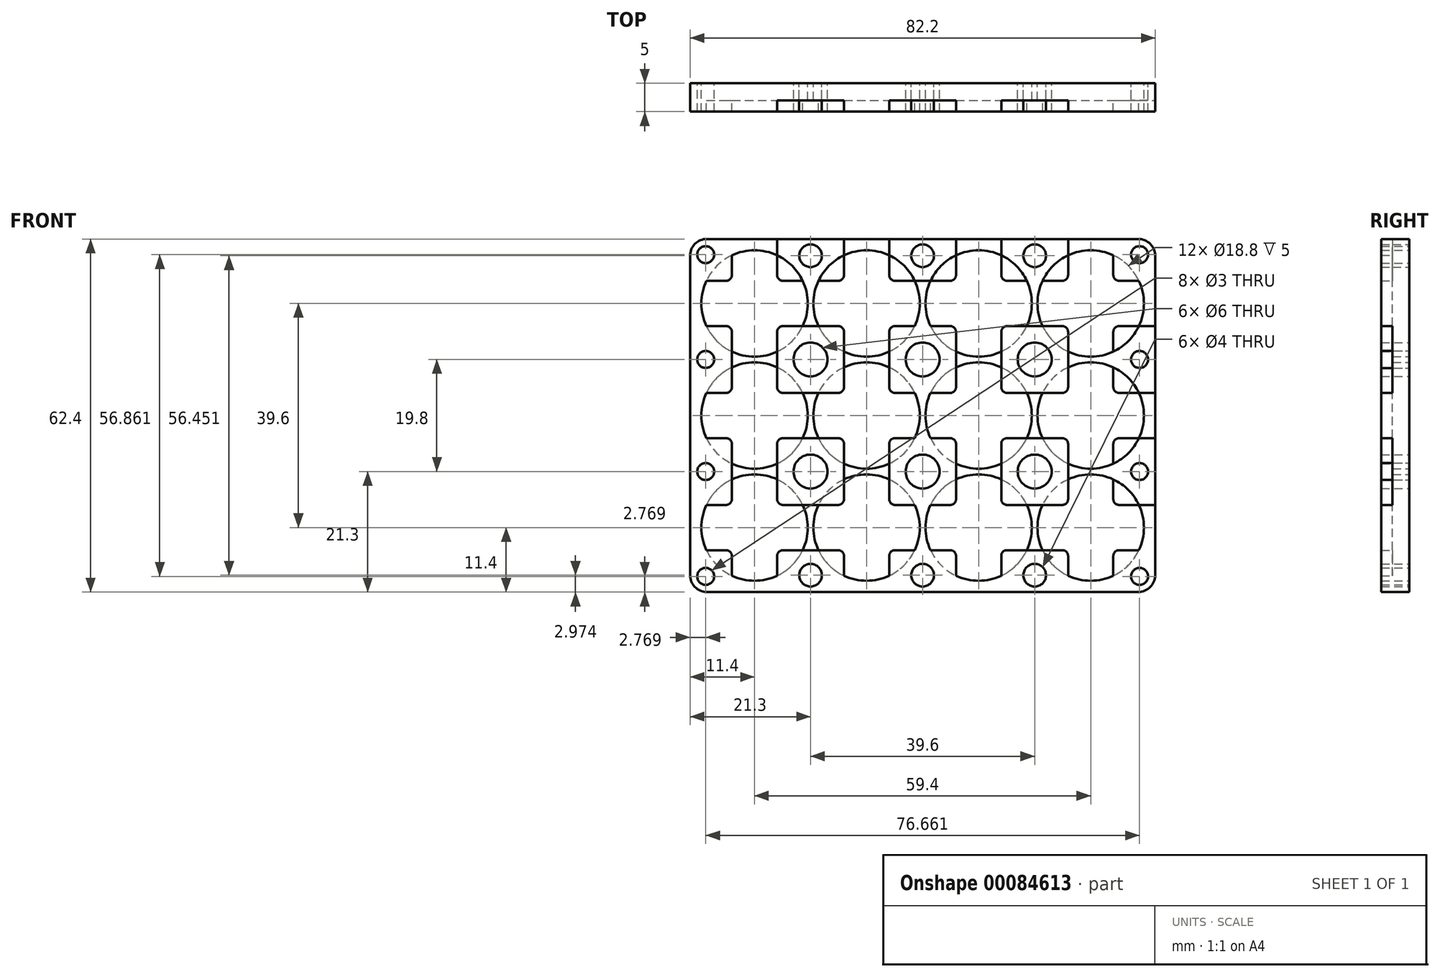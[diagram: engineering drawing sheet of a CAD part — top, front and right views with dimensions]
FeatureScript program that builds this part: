
annotation { "Feature Type Name" : "Feature", "Feature Type Description" : "" }
export const myFeature = defineFeature(function(context is Context, id is Id, definition is map)
    precondition{}
    {
        {
            var Q0;
            Q0=qCreatedBy(makeId("Front.planeOp"),FACE);
            var sketch = newSketch(context, id + "F0", { "sketchPlane" : qUnion([Q0]) });
            skCircle(sketch, "E0", {"center": v(0, 0) * mm, "radius": 9.4 * mm});
            skCircle(sketch, "E1.0.1.0", {"center": v(0, 19.8) * mm, "radius": 9.4 * mm});
            skCircle(sketch, "E1.0.2.0", {"center": v(0, 39.6) * mm, "radius": 9.4 * mm});
            skCircle(sketch, "E1.1.0.0", {"center": v(19.8, 0) * mm, "radius": 9.4 * mm});
            skCircle(sketch, "E1.1.1.0", {"center": v(19.8, 19.8) * mm, "radius": 9.4 * mm});
            skCircle(sketch, "E1.1.2.0", {"center": v(19.8, 39.6) * mm, "radius": 9.4 * mm});
            skCircle(sketch, "E1.2.0.0", {"center": v(39.6, 0) * mm, "radius": 9.4 * mm});
            skCircle(sketch, "E1.2.1.0", {"center": v(39.6, 19.8) * mm, "radius": 9.4 * mm});
            skCircle(sketch, "E1.2.2.0", {"center": v(39.6, 39.6) * mm, "radius": 9.4 * mm});
            skCircle(sketch, "E1.3.0.0", {"center": v(59.4, 0) * mm, "radius": 9.4 * mm});
            skCircle(sketch, "E1.3.1.0", {"center": v(59.4, 19.8) * mm, "radius": 9.4 * mm});
            skCircle(sketch, "E1.3.2.0", {"center": v(59.4, 39.6) * mm, "radius": 9.4 * mm});
            skLineSegment(sketch, "E1.direction1", {"start": v(0, 0) * mm, "end": v(19.8, 0) * mm, "construction": true});
            skLineSegment(sketch, "E1.direction2", {"start": v(0, 0) * mm, "end": v(0, 19.8) * mm, "construction": true});
            skLineSegment(sketch, "E2", {"start": v(-9.4, 19.8) * mm, "end": v(68.8, 19.8) * mm, "construction": true});
            skLineSegment(sketch, "E3", {"start": v(29.7, 19.8) * mm, "end": v(29.7, -16.3) * mm, "construction": true});
            skLineSegment(sketch, "E4.bottom", {"start": v(70.8, -11.4) * mm, "end": v(-11.4, -11.4) * mm});
            skLineSegment(sketch, "E4.top", {"start": v(70.8, 51) * mm, "end": v(-11.4, 51) * mm});
            skLineSegment(sketch, "E4.left", {"start": v(70.8, -11.4) * mm, "end": v(70.8, 51) * mm});
            skLineSegment(sketch, "E4.right", {"start": v(-11.4, -11.4) * mm, "end": v(-11.4, 51) * mm});
            skPoint(sketch, "E4.middle", {"position": v(29.7, 19.8) * mm});
            skLineSegment(sketch, "E5", {"start": v(19.8, 19.8) * mm, "end": v(0, 0) * mm, "construction": true});
            skLineSegment(sketch, "E6", {"start": v(19.8, 0) * mm, "end": v(0, 19.8) * mm, "construction": true});
            skCircle(sketch, "E7", {"center": v(9.9, 9.9) * mm, "radius": 3 * mm});
            skCircle(sketch, "E8.0.1.0", {"center": v(9.9, 29.7) * mm, "radius": 3 * mm});
            skCircle(sketch, "E8.1.0.0", {"center": v(29.7, 9.9) * mm, "radius": 3 * mm});
            skCircle(sketch, "E8.1.1.0", {"center": v(29.7, 29.7) * mm, "radius": 3 * mm});
            skCircle(sketch, "E8.2.0.0", {"center": v(49.5, 9.9) * mm, "radius": 3 * mm});
            skCircle(sketch, "E8.2.1.0", {"center": v(49.5, 29.7) * mm, "radius": 3 * mm});
            skLineSegment(sketch, "E8.direction1", {"start": v(9.9, 9.9) * mm, "end": v(29.7, 9.9) * mm, "construction": true});
            skLineSegment(sketch, "E8.direction2", {"start": v(9.9, 9.9) * mm, "end": v(9.9, 29.7) * mm, "construction": true});
            skLineSegment(sketch, "E9", {"start": v(9.9, 0) * mm, "end": v(9.9, -11.4) * mm, "construction": true});
            skCircle(sketch, "E10", {"center": v(9.9, -8.43) * mm, "radius": 2 * mm});
            skCircle(sketch, "E11.1.0.0", {"center": v(29.7, -8.43) * mm, "radius": 2 * mm});
            skCircle(sketch, "E11.2.0.0", {"center": v(49.5, -8.43) * mm, "radius": 2 * mm});
            skLineSegment(sketch, "E11.direction1", {"start": v(9.9, -8.43) * mm, "end": v(29.7, -8.43) * mm, "construction": true});
            skCircle(sketch, "E12.MirrorC", {"center": v(9.9, 48.03) * mm, "radius": 2 * mm});
            skCircle(sketch, "E13.MirrorC", {"center": v(29.7, 48.03) * mm, "radius": 2 * mm});
            skCircle(sketch, "E14.MirrorC", {"center": v(49.5, 48.03) * mm, "radius": 2 * mm});
            skLineSegment(sketch, "E15", {"start": v(0, 0) * mm, "end": v(-11.4, -11.4) * mm, "construction": true});
            skCircle(sketch, "E16", {"center": v(-8.63, -8.63) * mm, "radius": 1.5 * mm});
            skCircle(sketch, "E17", {"center": v(-8.63, 9.9) * mm, "radius": 1.5 * mm});
            skCircle(sketch, "E18", {"center": v(-8.63, 29.7) * mm, "radius": 1.5 * mm});
            skCircle(sketch, "E19.MirrorC", {"center": v(-8.63, 48.23) * mm, "radius": 1.5 * mm});
            skCircle(sketch, "E20.MirrorC", {"center": v(68.03, -8.63) * mm, "radius": 1.5 * mm});
            skCircle(sketch, "E21.MirrorC", {"center": v(68.03, 9.9) * mm, "radius": 1.5 * mm});
            skCircle(sketch, "E22.MirrorC", {"center": v(68.03, 29.7) * mm, "radius": 1.5 * mm});
            skCircle(sketch, "E23.MirrorC", {"center": v(68.03, 48.23) * mm, "radius": 1.5 * mm});
            skSolve(sketch);
        }
        {
            var Q0;
            Q0=qSketchRegion(id+"F0",true);
            extrude(context, id + "F1", {"entities" : qUnion([Q0]), "depth" : 3 * mm});
        }
        {
            var Q0;
            Q0=makeQuery(id+"F1.opExtrude","SWEPT_EDGE",EDGE,{"disambiguationData":[OSD([sQuery(id+"F0.wireOp",EDGE,"E4.top"),sQuery(id+"F0.wireOp",EDGE,"E4.left")])]});
            var Q1;
            Q1=makeQuery(id+"F1.opExtrude","SWEPT_EDGE",EDGE,{"disambiguationData":[OSD([sQuery(id+"F0.wireOp",EDGE,"E4.top"),sQuery(id+"F0.wireOp",EDGE,"E4.right")])]});
            var Q2;
            Q2=makeQuery(id+"F1.opExtrude","SWEPT_EDGE",EDGE,{"disambiguationData":[OSD([sQuery(id+"F0.wireOp",EDGE,"E4.bottom"),sQuery(id+"F0.wireOp",EDGE,"E4.right")])]});
            var Q3;
            Q3=makeQuery(id+"F1.opExtrude","SWEPT_EDGE",EDGE,{"disambiguationData":[OSD([sQuery(id+"F0.wireOp",EDGE,"E4.bottom"),sQuery(id+"F0.wireOp",EDGE,"E4.left")])]});
            fillet(context, id + "F2", {"entities" : qUnion([Q0, Q1, Q2, Q3]), "radius" : 3 * mm, "tangentPropagation" : true, "conicFillet" : false});
        }
        {
            var Q0;
            Q0=makeQuery(id+"F1.opExtrude","CAP_FACE",FACE,{"disambiguationData":[OSD([sQuery(id+"F0.wireOp",EDGE,"E0"),sQuery(id+"F0.wireOp",EDGE,"E1.0.1.0"),sQuery(id+"F0.wireOp",EDGE,"E1.0.2.0"),sQuery(id+"F0.wireOp",EDGE,"E1.1.0.0"),sQuery(id+"F0.wireOp",EDGE,"E1.1.1.0"),sQuery(id+"F0.wireOp",EDGE,"E1.1.2.0"),sQuery(id+"F0.wireOp",EDGE,"E1.2.0.0"),sQuery(id+"F0.wireOp",EDGE,"E1.2.1.0"),sQuery(id+"F0.wireOp",EDGE,"E1.2.2.0"),sQuery(id+"F0.wireOp",EDGE,"E1.3.0.0"),sQuery(id+"F0.wireOp",EDGE,"E1.3.1.0"),sQuery(id+"F0.wireOp",EDGE,"E1.3.2.0"),sQuery(id+"F0.wireOp",EDGE,"E4.bottom"),sQuery(id+"F0.wireOp",EDGE,"E4.top"),sQuery(id+"F0.wireOp",EDGE,"E4.left"),sQuery(id+"F0.wireOp",EDGE,"E4.right"),sQuery(id+"F0.wireOp",EDGE,"E7"),sQuery(id+"F0.wireOp",EDGE,"E8.0.1.0"),sQuery(id+"F0.wireOp",EDGE,"E8.1.0.0"),sQuery(id+"F0.wireOp",EDGE,"E8.1.1.0"),sQuery(id+"F0.wireOp",EDGE,"E8.2.0.0"),sQuery(id+"F0.wireOp",EDGE,"E8.2.1.0"),sQuery(id+"F0.wireOp",EDGE,"E10"),sQuery(id+"F0.wireOp",EDGE,"E11.1.0.0"),sQuery(id+"F0.wireOp",EDGE,"E11.2.0.0"),sQuery(id+"F0.wireOp",EDGE,"E12.MirrorC"),sQuery(id+"F0.wireOp",EDGE,"E13.MirrorC"),sQuery(id+"F0.wireOp",EDGE,"E14.MirrorC"),sQuery(id+"F0.wireOp",EDGE,"E16"),sQuery(id+"F0.wireOp",EDGE,"E17"),sQuery(id+"F0.wireOp",EDGE,"E18"),sQuery(id+"F0.wireOp",EDGE,"E19.MirrorC"),sQuery(id+"F0.wireOp",EDGE,"E20.MirrorC"),sQuery(id+"F0.wireOp",EDGE,"E21.MirrorC"),sQuery(id+"F0.wireOp",EDGE,"E22.MirrorC"),sQuery(id+"F0.wireOp",EDGE,"E23.MirrorC")])],"isStart":false});
            var sketch = newSketch(context, id + "F3", { "sketchPlane" : qUnion([Q0]) });
            skLineSegment(sketch, "E24.0", {"start": v(67.8, 51) * mm, "end": v(-8.4, 51) * mm});
            skArc(sketch, "E24.1", {"start": v(-8.4, 51) * mm, "mid": v(-10.52, 50.12) * mm, "end": v(-11.4, 48) * mm});
            skLineSegment(sketch, "E24.2", {"start": v(-11.4, -8.4) * mm, "end": v(-11.4, 35.6) * mm});
            skArc(sketch, "E24.3", {"start": v(-11.4, -8.4) * mm, "mid": v(-10.52, -10.52) * mm, "end": v(-8.4, -11.4) * mm});
            skLineSegment(sketch, "E24.4", {"start": v(67.8, -11.4) * mm, "end": v(-8.4, -11.4) * mm});
            skArc(sketch, "E24.5", {"start": v(67.8, -11.4) * mm, "mid": v(69.92, -10.52) * mm, "end": v(70.8, -8.4) * mm});
            skLineSegment(sketch, "E24.6", {"start": v(70.8, -8.4) * mm, "end": v(70.8, 48) * mm});
            skArc(sketch, "E24.7", {"start": v(70.8, 48) * mm, "mid": v(69.92, 50.12) * mm, "end": v(67.8, 51) * mm});
            skCircle(sketch, "E24.8", {"center": v(59.4, 39.6) * mm, "radius": 9.4 * mm});
            skCircle(sketch, "E24.9", {"center": v(39.6, 39.6) * mm, "radius": 9.4 * mm});
            skCircle(sketch, "E24.10", {"center": v(19.8, 39.6) * mm, "radius": 9.4 * mm});
            skArc(sketch, "E24.11", {"start": v(-8.5, 43.6) * mm, "mid": v(-9.4, 39.6) * mm, "end": v(-8.5, 35.6) * mm});
            skCircle(sketch, "E24.12", {"center": v(0, 19.8) * mm, "radius": 9.4 * mm});
            skCircle(sketch, "E24.13", {"center": v(19.8, 19.8) * mm, "radius": 9.4 * mm});
            skCircle(sketch, "E24.14", {"center": v(39.6, 19.8) * mm, "radius": 9.4 * mm});
            skCircle(sketch, "E24.15", {"center": v(59.4, 19.8) * mm, "radius": 9.4 * mm});
            skCircle(sketch, "E24.16", {"center": v(59.4, 0) * mm, "radius": 9.4 * mm});
            skCircle(sketch, "E24.17", {"center": v(39.6, 0) * mm, "radius": 9.4 * mm});
            skCircle(sketch, "E24.18", {"center": v(19.8, 0) * mm, "radius": 9.4 * mm});
            skCircle(sketch, "E24.19", {"center": v(0, 0) * mm, "radius": 9.4 * mm});
            skLineSegment(sketch, "E25.left", {"start": v(-11.4, 39.6) * mm, "end": v(-11.4, 43.6) * mm});
            skLineSegment(sketch, "E25.right", {"start": v(70.8, 39.6) * mm, "end": v(70.8, 43.6) * mm});
            skLineSegment(sketch, "E26.trimOffspring", {"start": v(-11.4, 43.6) * mm, "end": v(-11.4, 48) * mm});
            skLineSegment(sketch, "E27", {"start": v(-4, 51) * mm, "end": v(-4, 43.6) * mm});
            skLineSegment(sketch, "E28.MirrorCS", {"start": v(4, 51) * mm, "end": v(4, 43.6) * mm});
            skLineSegment(sketch, "E29", {"start": v(-11.4, -4) * mm, "end": v(-4, -4) * mm});
            skLineSegment(sketch, "E30.MirrorCS", {"start": v(-11.4, 4) * mm, "end": v(-4, 4) * mm});
            skLineSegment(sketch, "E31.1.0.0", {"start": v(15.8, 51) * mm, "end": v(15.8, 43.6) * mm});
            skLineSegment(sketch, "E31.1.0.1", {"start": v(23.8, 51) * mm, "end": v(23.8, 43.6) * mm});
            skLineSegment(sketch, "E31.2.0.0", {"start": v(35.6, 51) * mm, "end": v(35.6, 43.6) * mm});
            skLineSegment(sketch, "E31.2.0.1", {"start": v(43.6, 51) * mm, "end": v(43.6, 43.6) * mm});
            skLineSegment(sketch, "E31.3.0.0", {"start": v(55.4, 51) * mm, "end": v(55.4, 43.6) * mm});
            skLineSegment(sketch, "E31.3.0.1", {"start": v(63.4, 51) * mm, "end": v(63.4, 43.6) * mm});
            skLineSegment(sketch, "E31.direction1", {"start": v(-4, -11.4) * mm, "end": v(15.8, -11.4) * mm, "construction": true});
            skLineSegment(sketch, "E32.0.1.0", {"start": v(-11.4, 23.8) * mm, "end": v(-4, 23.8) * mm});
            skLineSegment(sketch, "E32.0.1.1", {"start": v(-11.4, 15.8) * mm, "end": v(-4, 15.8) * mm});
            skLineSegment(sketch, "E32.0.2.0", {"start": v(-11.4, 43.6) * mm, "end": v(-4, 43.6) * mm});
            skLineSegment(sketch, "E32.0.2.1", {"start": v(-11.4, 35.6) * mm, "end": v(-4, 35.6) * mm});
            skLineSegment(sketch, "E32.direction1", {"start": v(-11.4, 4) * mm, "end": v(-4, 4) * mm, "construction": true});
            skLineSegment(sketch, "E32.direction2", {"start": v(-11.4, 4) * mm, "end": v(-11.4, 23.8) * mm, "construction": true});
            skLineSegment(sketch, "E33.trimOffspring", {"start": v(4, 35.6) * mm, "end": v(15.8, 35.6) * mm});
            skLineSegment(sketch, "E34.trimOffspring", {"start": v(4, 43.6) * mm, "end": v(15.8, 43.6) * mm});
            skLineSegment(sketch, "E35.trimOffspring", {"start": v(4, 35.6) * mm, "end": v(4, 23.8) * mm});
            skLineSegment(sketch, "E36.trimOffspring", {"start": v(-4, 35.6) * mm, "end": v(-4, 23.8) * mm});
            skLineSegment(sketch, "E37.trimOffspring", {"start": v(15.8, 35.6) * mm, "end": v(15.8, 23.8) * mm});
            skLineSegment(sketch, "E38.trimOffspring", {"start": v(23.8, 35.6) * mm, "end": v(23.8, 23.8) * mm});
            skLineSegment(sketch, "E39.trimOffspring", {"start": v(35.6, 35.6) * mm, "end": v(35.6, 23.8) * mm});
            skLineSegment(sketch, "E40.trimOffspring", {"start": v(43.6, 35.6) * mm, "end": v(43.6, 23.8) * mm});
            skLineSegment(sketch, "E41.trimOffspring", {"start": v(55.4, 35.6) * mm, "end": v(55.4, 23.8) * mm});
            skLineSegment(sketch, "E42.trimOffspring", {"start": v(63.4, 35.6) * mm, "end": v(63.4, 23.8) * mm});
            skLineSegment(sketch, "E43.trimOffspring", {"start": v(23.8, 43.6) * mm, "end": v(35.6, 43.6) * mm});
            skLineSegment(sketch, "E44.trimOffspring", {"start": v(43.6, 43.6) * mm, "end": v(55.4, 43.6) * mm});
            skLineSegment(sketch, "E45.trimOffspring", {"start": v(63.4, 43.6) * mm, "end": v(70.8, 43.6) * mm});
            skLineSegment(sketch, "E46.trimOffspring", {"start": v(63.4, 35.6) * mm, "end": v(70.8, 35.6) * mm});
            skLineSegment(sketch, "E47.trimOffspring", {"start": v(43.6, 35.6) * mm, "end": v(55.4, 35.6) * mm});
            skLineSegment(sketch, "E48.trimOffspring", {"start": v(23.8, 35.6) * mm, "end": v(35.6, 35.6) * mm});
            skLineSegment(sketch, "E49.trimOffspring", {"start": v(4, 23.8) * mm, "end": v(15.8, 23.8) * mm});
            skLineSegment(sketch, "E50.trimOffspring", {"start": v(4, 15.8) * mm, "end": v(11.3, 15.8) * mm});
            skLineSegment(sketch, "E51.trimOffspring", {"start": v(-4, 15.8) * mm, "end": v(-4, 4) * mm});
            skLineSegment(sketch, "E52.trimOffspring", {"start": v(4, 15.8) * mm, "end": v(4, 4) * mm});
            skLineSegment(sketch, "E53.trimOffspring", {"start": v(15.8, 15.8) * mm, "end": v(15.8, 4) * mm});
            skLineSegment(sketch, "E54.trimOffspring", {"start": v(23.8, 15.8) * mm, "end": v(23.8, 4) * mm});
            skLineSegment(sketch, "E55.trimOffspring", {"start": v(35.6, 15.8) * mm, "end": v(35.6, 4) * mm});
            skLineSegment(sketch, "E56.trimOffspring", {"start": v(43.6, 15.8) * mm, "end": v(43.6, 4) * mm});
            skLineSegment(sketch, "E57.trimOffspring", {"start": v(55.4, 15.8) * mm, "end": v(55.4, 4) * mm});
            skLineSegment(sketch, "E58.trimOffspring", {"start": v(63.4, 15.8) * mm, "end": v(63.4, 4) * mm});
            skLineSegment(sketch, "E59.trimOffspring", {"start": v(23.8, 23.8) * mm, "end": v(35.6, 23.8) * mm});
            skLineSegment(sketch, "E60.trimOffspring", {"start": v(43.6, 23.8) * mm, "end": v(55.4, 23.8) * mm});
            skLineSegment(sketch, "E61.trimOffspring", {"start": v(63.4, 23.8) * mm, "end": v(70.8, 23.8) * mm});
            skLineSegment(sketch, "E62.trimOffspring", {"start": v(23.8, 15.8) * mm, "end": v(35.6, 15.8) * mm});
            skLineSegment(sketch, "E63.trimOffspring", {"start": v(63.4, 15.8) * mm, "end": v(70.8, 15.8) * mm});
            skLineSegment(sketch, "E64.trimOffspring", {"start": v(63.4, 4) * mm, "end": v(70.8, 4) * mm});
            skLineSegment(sketch, "E65.trimOffspring", {"start": v(43.6, 4) * mm, "end": v(55.4, 4) * mm});
            skLineSegment(sketch, "E66.trimOffspring", {"start": v(23.8, 4) * mm, "end": v(35.6, 4) * mm});
            skLineSegment(sketch, "E67.trimOffspring", {"start": v(4, 4) * mm, "end": v(15.8, 4) * mm});
            skLineSegment(sketch, "E68.trimOffspring", {"start": v(4, -4) * mm, "end": v(11.3, -4) * mm});
            skLineSegment(sketch, "E69.trimOffspring", {"start": v(23.8, -4) * mm, "end": v(35.6, -4) * mm});
            skLineSegment(sketch, "E70.trimOffspring", {"start": v(63.4, -4) * mm, "end": v(70.8, -4) * mm});
            skLineSegment(sketch, "E71.trimOffspring", {"start": v(55.4, -4) * mm, "end": v(55.4, -11.4) * mm});
            skLineSegment(sketch, "E72.trimOffspring", {"start": v(63.4, -4) * mm, "end": v(63.4, -11.4) * mm});
            skLineSegment(sketch, "E73.trimOffspring", {"start": v(43.6, -4) * mm, "end": v(43.6, -11.4) * mm});
            skLineSegment(sketch, "E74.trimOffspring", {"start": v(35.6, -4) * mm, "end": v(35.6, -11.4) * mm});
            skLineSegment(sketch, "E75.trimOffspring", {"start": v(23.8, -4) * mm, "end": v(23.8, -11.4) * mm});
            skLineSegment(sketch, "E76.trimOffspring", {"start": v(4, -4) * mm, "end": v(4, -11.4) * mm});
            skLineSegment(sketch, "E77.trimOffspring", {"start": v(-4, -4) * mm, "end": v(-4, -11.4) * mm});
            skLineSegment(sketch, "E78", {"start": v(11.3, 15.8) * mm, "end": v(15.8, 15.8) * mm});
            skLineSegment(sketch, "E79", {"start": v(11.3, -4) * mm, "end": v(15.8, -4) * mm});
            skLineSegment(sketch, "E80.trimOffspring", {"start": v(15.8, -4) * mm, "end": v(15.8, -11.4) * mm});
            skLineSegment(sketch, "E81.trimOffspring", {"start": v(43.6, 15.8) * mm, "end": v(55.4, 15.8) * mm});
            skLineSegment(sketch, "E82.trimOffspring", {"start": v(4, 4) * mm, "end": v(13.6, 4) * mm, "construction": true});
            skLineSegment(sketch, "E83.trimOffspring", {"start": v(43.6, -4) * mm, "end": v(55.4, -4) * mm});
            skArc(sketch, "E84.trimOffspring", {"start": v(4, 48.1) * mm, "mid": v(0, 49) * mm, "end": v(-4, 48.1) * mm});
            skArc(sketch, "E85.trimOffspring", {"start": v(8.5, 35.6) * mm, "mid": v(9.4, 39.6) * mm, "end": v(8.5, 43.6) * mm});
            skArc(sketch, "E86.trimOffspring", {"start": v(-4, 31.1) * mm, "mid": v(0, 30.2) * mm, "end": v(4, 31.1) * mm});
            skSolve(sketch);
        }
        {
            var Q0;
            {var subQ6=sQuery(id+"F3.wireOp",EDGE,"E24.1");Q0=makeQuery(id+"F3.imprint","IMPRINT",FACE,{"disambiguationData":[TD([[makeQuery(id+"F3.imprint","IMPRINT",EDGE,{"derivedFrom":subQ6}),1.0]])]});}
            var Q1;
            {var subQ0=sQuery(id+"F3.wireOp",EDGE,"E32.0.2.0");var subQ1=sQuery(id+"F3.wireOp",EDGE,"E27");var subQ2=makeQuery(id+"F3.imprint","INTERSECT",VERTEX,{"derivedFrom":[subQ1,subQ0]});Q1=makeQuery(id+"F3.imprint","IMPRINT",FACE,{"disambiguationData":[TD([[makeQuery(id+"F3.imprint","IMPRINT",EDGE,{"disambiguationData":[TD([[subQ2,1.0]])],"derivedFrom":subQ1}),-1.0]])]});}
            var Q2;
            {var subQ0=sQuery(id+"F3.wireOp",EDGE,"E34.trimOffspring");var subQ1=sQuery(id+"F3.wireOp",EDGE,"E28.MirrorCS");var subQ2=makeQuery(id+"F3.imprint","INTERSECT",VERTEX,{"derivedFrom":[subQ1,subQ0]});Q2=makeQuery(id+"F3.imprint","IMPRINT",FACE,{"disambiguationData":[TD([[makeQuery(id+"F3.imprint","IMPRINT",EDGE,{"disambiguationData":[TD([[subQ2,1.0]])],"derivedFrom":subQ1}),1.0]])]});}
            var Q3;
            Q3=makeQuery(id+"F3.imprint","IMPRINT",FACE,{"disambiguationData":[TD([[makeQuery(id+"F3.imprint","IMPRINT",EDGE,{"derivedFrom":makeQuery(id+"F1.opExtrude","CAP_EDGE",EDGE,{"disambiguationData":[OSD([sQuery(id+"F0.wireOp",EDGE,"E12.MirrorC")])],"isStart":false})}),1.0]])]});
            var Q4;
            {var subQ0=sQuery(id+"F3.wireOp",EDGE,"E34.trimOffspring");var subQ1=sQuery(id+"F3.wireOp",EDGE,"E31.1.0.0");var subQ2=makeQuery(id+"F3.imprint","INTERSECT",VERTEX,{"derivedFrom":[subQ1,subQ0]});Q4=makeQuery(id+"F3.imprint","IMPRINT",FACE,{"disambiguationData":[TD([[makeQuery(id+"F3.imprint","IMPRINT",EDGE,{"disambiguationData":[TD([[subQ2,1.0]])],"derivedFrom":subQ1}),-1.0]])]});}
            var Q5;
            {var subQ0=sQuery(id+"F3.wireOp",EDGE,"E43.trimOffspring");var subQ1=sQuery(id+"F3.wireOp",EDGE,"E31.1.0.1");var subQ2=makeQuery(id+"F3.imprint","INTERSECT",VERTEX,{"derivedFrom":[subQ1,subQ0]});Q5=makeQuery(id+"F3.imprint","IMPRINT",FACE,{"disambiguationData":[TD([[makeQuery(id+"F3.imprint","IMPRINT",EDGE,{"disambiguationData":[TD([[subQ2,1.0]])],"derivedFrom":subQ1}),1.0]])]});}
            var Q6;
            Q6=makeQuery(id+"F3.imprint","IMPRINT",FACE,{"disambiguationData":[TD([[makeQuery(id+"F3.imprint","IMPRINT",EDGE,{"derivedFrom":makeQuery(id+"F1.opExtrude","CAP_EDGE",EDGE,{"disambiguationData":[OSD([sQuery(id+"F0.wireOp",EDGE,"E13.MirrorC")])],"isStart":false})}),1.0]])]});
            var Q7;
            {var subQ0=sQuery(id+"F3.wireOp",EDGE,"E31.2.0.0");var subQ1=sQuery(id+"F3.wireOp",EDGE,"E24.9");var subQ2=makeQuery(id+"F3.imprint","INTERSECT",VERTEX,{"derivedFrom":[subQ1,subQ0]});Q7=makeQuery(id+"F3.imprint","IMPRINT",FACE,{"disambiguationData":[TD([[makeQuery(id+"F3.imprint","IMPRINT",EDGE,{"disambiguationData":[TD([[subQ2,-1.0]])],"derivedFrom":subQ1}),1.0]])]});}
            var Q8;
            {var subQ0=sQuery(id+"F3.wireOp",EDGE,"E31.2.0.1");var subQ1=sQuery(id+"F3.wireOp",EDGE,"E24.9");var subQ2=makeQuery(id+"F3.imprint","INTERSECT",VERTEX,{"derivedFrom":[subQ1,subQ0]});Q8=makeQuery(id+"F3.imprint","IMPRINT",FACE,{"disambiguationData":[TD([[makeQuery(id+"F3.imprint","IMPRINT",EDGE,{"disambiguationData":[TD([[subQ2,1.0]])],"derivedFrom":subQ1}),1.0]])]});}
            var Q9;
            Q9=makeQuery(id+"F3.imprint","IMPRINT",FACE,{"disambiguationData":[TD([[makeQuery(id+"F3.imprint","IMPRINT",EDGE,{"derivedFrom":makeQuery(id+"F1.opExtrude","CAP_EDGE",EDGE,{"disambiguationData":[OSD([sQuery(id+"F0.wireOp",EDGE,"E14.MirrorC")])],"isStart":false})}),1.0]])]});
            var Q10;
            {var subQ0=sQuery(id+"F3.wireOp",EDGE,"E44.trimOffspring");var subQ1=sQuery(id+"F3.wireOp",EDGE,"E31.3.0.0");var subQ2=makeQuery(id+"F3.imprint","INTERSECT",VERTEX,{"derivedFrom":[subQ1,subQ0]});Q10=makeQuery(id+"F3.imprint","IMPRINT",FACE,{"disambiguationData":[TD([[makeQuery(id+"F3.imprint","IMPRINT",EDGE,{"disambiguationData":[TD([[subQ2,1.0]])],"derivedFrom":subQ1}),-1.0]])]});}
            var Q11;
            {var subQ0=sQuery(id+"F3.wireOp",EDGE,"E45.trimOffspring");var subQ1=sQuery(id+"F3.wireOp",EDGE,"E31.3.0.1");var subQ2=makeQuery(id+"F3.imprint","INTERSECT",VERTEX,{"derivedFrom":[subQ1,subQ0]});Q11=makeQuery(id+"F3.imprint","IMPRINT",FACE,{"disambiguationData":[TD([[makeQuery(id+"F3.imprint","IMPRINT",EDGE,{"disambiguationData":[TD([[subQ2,1.0]])],"derivedFrom":subQ1}),1.0]])]});}
            var Q12;
            {var subQ9=sQuery(id+"F3.wireOp",EDGE,"E24.7");Q12=makeQuery(id+"F3.imprint","IMPRINT",FACE,{"disambiguationData":[TD([[makeQuery(id+"F3.imprint","IMPRINT",EDGE,{"derivedFrom":subQ9}),1.0]])]});}
            var Q13;
            {var subQ0=sQuery(id+"F3.wireOp",EDGE,"E61.trimOffspring");var subQ1=sQuery(id+"F3.wireOp",EDGE,"E42.trimOffspring");var subQ2=makeQuery(id+"F3.imprint","INTERSECT",VERTEX,{"derivedFrom":[subQ1,subQ0]});Q13=makeQuery(id+"F3.imprint","IMPRINT",FACE,{"disambiguationData":[TD([[makeQuery(id+"F3.imprint","IMPRINT",EDGE,{"disambiguationData":[TD([[subQ2,1.0]])],"derivedFrom":subQ1}),1.0]])]});}
            var Q14;
            Q14=makeQuery(id+"F3.imprint","IMPRINT",FACE,{"disambiguationData":[TD([[makeQuery(id+"F3.imprint","IMPRINT",EDGE,{"derivedFrom":makeQuery(id+"F1.opExtrude","CAP_EDGE",EDGE,{"disambiguationData":[OSD([sQuery(id+"F0.wireOp",EDGE,"E22.MirrorC")])],"isStart":false})}),1.0]])]});
            var Q15;
            {var subQ0=sQuery(id+"F3.wireOp",EDGE,"E46.trimOffspring");var subQ1=sQuery(id+"F3.wireOp",EDGE,"E42.trimOffspring");var subQ2=makeQuery(id+"F3.imprint","INTERSECT",VERTEX,{"derivedFrom":[subQ1,subQ0]});Q15=makeQuery(id+"F3.imprint","IMPRINT",FACE,{"disambiguationData":[TD([[makeQuery(id+"F3.imprint","IMPRINT",EDGE,{"disambiguationData":[TD([[subQ2,-1.0]])],"derivedFrom":subQ1}),1.0]])]});}
            var Q16;
            {var subQ0=sQuery(id+"F3.wireOp",EDGE,"E60.trimOffspring");var subQ1=sQuery(id+"F3.wireOp",EDGE,"E41.trimOffspring");var subQ2=makeQuery(id+"F3.imprint","INTERSECT",VERTEX,{"derivedFrom":[subQ1,subQ0]});Q16=makeQuery(id+"F3.imprint","IMPRINT",FACE,{"disambiguationData":[TD([[makeQuery(id+"F3.imprint","IMPRINT",EDGE,{"disambiguationData":[TD([[subQ2,1.0]])],"derivedFrom":subQ1}),-1.0]])]});}
            var Q17;
            {var subQ0=sQuery(id+"F3.wireOp",EDGE,"E60.trimOffspring");var subQ1=sQuery(id+"F3.wireOp",EDGE,"E40.trimOffspring");var subQ2=makeQuery(id+"F3.imprint","INTERSECT",VERTEX,{"derivedFrom":[subQ1,subQ0]});Q17=makeQuery(id+"F3.imprint","IMPRINT",FACE,{"disambiguationData":[TD([[makeQuery(id+"F3.imprint","IMPRINT",EDGE,{"disambiguationData":[TD([[subQ2,1.0]])],"derivedFrom":subQ1}),1.0]])]});}
            var Q18;
            {var subQ0=sQuery(id+"F3.wireOp",EDGE,"E40.trimOffspring");var subQ1=sQuery(id+"F3.wireOp",EDGE,"E24.9");var subQ2=makeQuery(id+"F3.imprint","INTERSECT",VERTEX,{"derivedFrom":[subQ1,subQ0]});Q18=makeQuery(id+"F3.imprint","IMPRINT",FACE,{"disambiguationData":[TD([[makeQuery(id+"F3.imprint","IMPRINT",EDGE,{"disambiguationData":[TD([[subQ2,-1.0]])],"derivedFrom":subQ1}),1.0]])]});}
            var Q19;
            {var subQ0=sQuery(id+"F3.wireOp",EDGE,"E47.trimOffspring");var subQ1=sQuery(id+"F3.wireOp",EDGE,"E41.trimOffspring");var subQ2=makeQuery(id+"F3.imprint","INTERSECT",VERTEX,{"derivedFrom":[subQ1,subQ0]});Q19=makeQuery(id+"F3.imprint","IMPRINT",FACE,{"disambiguationData":[TD([[makeQuery(id+"F3.imprint","IMPRINT",EDGE,{"disambiguationData":[TD([[subQ2,-1.0]])],"derivedFrom":subQ1}),-1.0]])]});}
            var Q20;
            Q20=makeQuery(id+"F3.imprint","IMPRINT",FACE,{"disambiguationData":[TD([[makeQuery(id+"F3.imprint","IMPRINT",EDGE,{"derivedFrom":makeQuery(id+"F1.opExtrude","CAP_EDGE",EDGE,{"disambiguationData":[OSD([sQuery(id+"F0.wireOp",EDGE,"E8.2.1.0")])],"isStart":false})}),-1.0]])]});
            var Q21;
            {var subQ0=sQuery(id+"F3.wireOp",EDGE,"E48.trimOffspring");var subQ1=sQuery(id+"F3.wireOp",EDGE,"E38.trimOffspring");var subQ2=makeQuery(id+"F3.imprint","INTERSECT",VERTEX,{"derivedFrom":[subQ1,subQ0]});Q21=makeQuery(id+"F3.imprint","IMPRINT",FACE,{"disambiguationData":[TD([[makeQuery(id+"F3.imprint","IMPRINT",EDGE,{"disambiguationData":[TD([[subQ2,-1.0]])],"derivedFrom":subQ1}),1.0]])]});}
            var Q22;
            {var subQ0=sQuery(id+"F3.wireOp",EDGE,"E59.trimOffspring");var subQ1=sQuery(id+"F3.wireOp",EDGE,"E38.trimOffspring");var subQ2=makeQuery(id+"F3.imprint","INTERSECT",VERTEX,{"derivedFrom":[subQ1,subQ0]});Q22=makeQuery(id+"F3.imprint","IMPRINT",FACE,{"disambiguationData":[TD([[makeQuery(id+"F3.imprint","IMPRINT",EDGE,{"disambiguationData":[TD([[subQ2,1.0]])],"derivedFrom":subQ1}),1.0]])]});}
            var Q23;
            {var subQ0=sQuery(id+"F3.wireOp",EDGE,"E59.trimOffspring");var subQ1=sQuery(id+"F3.wireOp",EDGE,"E39.trimOffspring");var subQ2=makeQuery(id+"F3.imprint","INTERSECT",VERTEX,{"derivedFrom":[subQ1,subQ0]});Q23=makeQuery(id+"F3.imprint","IMPRINT",FACE,{"disambiguationData":[TD([[makeQuery(id+"F3.imprint","IMPRINT",EDGE,{"disambiguationData":[TD([[subQ2,1.0]])],"derivedFrom":subQ1}),-1.0]])]});}
            var Q24;
            {var subQ0=sQuery(id+"F3.wireOp",EDGE,"E48.trimOffspring");var subQ1=sQuery(id+"F3.wireOp",EDGE,"E24.9");var subQ2=makeQuery(id+"F3.imprint","INTERSECT",VERTEX,{"derivedFrom":[subQ1,subQ0]});Q24=makeQuery(id+"F3.imprint","IMPRINT",FACE,{"disambiguationData":[TD([[makeQuery(id+"F3.imprint","IMPRINT",EDGE,{"disambiguationData":[TD([[subQ2,-1.0]])],"derivedFrom":subQ1}),1.0]])]});}
            var Q25;
            Q25=makeQuery(id+"F3.imprint","IMPRINT",FACE,{"disambiguationData":[TD([[makeQuery(id+"F3.imprint","IMPRINT",EDGE,{"derivedFrom":makeQuery(id+"F1.opExtrude","CAP_EDGE",EDGE,{"disambiguationData":[OSD([sQuery(id+"F0.wireOp",EDGE,"E8.1.1.0")])],"isStart":false})}),-1.0]])]});
            var Q26;
            Q26=makeQuery(id+"F3.imprint","IMPRINT",FACE,{"disambiguationData":[TD([[makeQuery(id+"F3.imprint","IMPRINT",EDGE,{"derivedFrom":makeQuery(id+"F1.opExtrude","CAP_EDGE",EDGE,{"disambiguationData":[OSD([sQuery(id+"F0.wireOp",EDGE,"E8.0.1.0")])],"isStart":false})}),-1.0]])]});
            var Q27;
            {var subQ0=sQuery(id+"F3.wireOp",EDGE,"E35.trimOffspring");var subQ1=sQuery(id+"F3.wireOp",EDGE,"E33.trimOffspring");var subQ2=makeQuery(id+"F3.imprint","INTERSECT",VERTEX,{"derivedFrom":[subQ1,subQ0]});Q27=makeQuery(id+"F3.imprint","IMPRINT",FACE,{"disambiguationData":[TD([[makeQuery(id+"F3.imprint","IMPRINT",EDGE,{"disambiguationData":[TD([[subQ2,-1.0]])],"derivedFrom":subQ1}),-1.0]])]});}
            var Q28;
            {var subQ0=sQuery(id+"F3.wireOp",EDGE,"E37.trimOffspring");var subQ1=sQuery(id+"F3.wireOp",EDGE,"E33.trimOffspring");var subQ2=makeQuery(id+"F3.imprint","INTERSECT",VERTEX,{"derivedFrom":[subQ1,subQ0]});Q28=makeQuery(id+"F3.imprint","IMPRINT",FACE,{"disambiguationData":[TD([[makeQuery(id+"F3.imprint","IMPRINT",EDGE,{"disambiguationData":[TD([[subQ2,1.0]])],"derivedFrom":subQ1}),-1.0]])]});}
            var Q29;
            {var subQ0=sQuery(id+"F3.wireOp",EDGE,"E49.trimOffspring");var subQ1=sQuery(id+"F3.wireOp",EDGE,"E37.trimOffspring");var subQ2=makeQuery(id+"F3.imprint","INTERSECT",VERTEX,{"derivedFrom":[subQ1,subQ0]});Q29=makeQuery(id+"F3.imprint","IMPRINT",FACE,{"disambiguationData":[TD([[makeQuery(id+"F3.imprint","IMPRINT",EDGE,{"disambiguationData":[TD([[subQ2,1.0]])],"derivedFrom":subQ1}),-1.0]])]});}
            var Q30;
            {var subQ0=sQuery(id+"F3.wireOp",EDGE,"E49.trimOffspring");var subQ1=sQuery(id+"F3.wireOp",EDGE,"E35.trimOffspring");var subQ2=makeQuery(id+"F3.imprint","INTERSECT",VERTEX,{"derivedFrom":[subQ1,subQ0]});Q30=makeQuery(id+"F3.imprint","IMPRINT",FACE,{"disambiguationData":[TD([[makeQuery(id+"F3.imprint","IMPRINT",EDGE,{"disambiguationData":[TD([[subQ2,1.0]])],"derivedFrom":subQ1}),1.0]])]});}
            var Q31;
            Q31=makeQuery(id+"F3.imprint","IMPRINT",FACE,{"disambiguationData":[TD([[makeQuery(id+"F3.imprint","IMPRINT",EDGE,{"derivedFrom":makeQuery(id+"F1.opExtrude","CAP_EDGE",EDGE,{"disambiguationData":[OSD([sQuery(id+"F0.wireOp",EDGE,"E17")])],"isStart":false})}),-1.0]])]});
            var Q32;
            {var subQ0=sQuery(id+"F3.wireOp",EDGE,"E51.trimOffspring");var subQ1=sQuery(id+"F3.wireOp",EDGE,"E32.0.1.1");var subQ2=makeQuery(id+"F3.imprint","INTERSECT",VERTEX,{"derivedFrom":[subQ1,subQ0]});Q32=makeQuery(id+"F3.imprint","IMPRINT",FACE,{"disambiguationData":[TD([[makeQuery(id+"F3.imprint","IMPRINT",EDGE,{"disambiguationData":[TD([[subQ2,1.0]])],"derivedFrom":subQ1}),-1.0]])]});}
            var Q33;
            {var subQ0=sQuery(id+"F3.wireOp",EDGE,"E51.trimOffspring");var subQ1=sQuery(id+"F3.wireOp",EDGE,"E30.MirrorCS");var subQ2=makeQuery(id+"F3.imprint","INTERSECT",VERTEX,{"derivedFrom":[subQ1,subQ0]});Q33=makeQuery(id+"F3.imprint","IMPRINT",FACE,{"disambiguationData":[TD([[makeQuery(id+"F3.imprint","IMPRINT",EDGE,{"disambiguationData":[TD([[subQ2,1.0]])],"derivedFrom":subQ1}),1.0]])]});}
            var Q34;
            {var subQ1=sQuery(id+"F3.wireOp",EDGE,"E24.3");Q34=makeQuery(id+"F3.imprint","IMPRINT",FACE,{"disambiguationData":[TD([[makeQuery(id+"F3.imprint","IMPRINT",EDGE,{"derivedFrom":subQ1}),1.0]])]});}
            var Q35;
            {var subQ0=sQuery(id+"F3.wireOp",EDGE,"E77.trimOffspring");var subQ1=sQuery(id+"F3.wireOp",EDGE,"E29");var subQ2=makeQuery(id+"F3.imprint","INTERSECT",VERTEX,{"derivedFrom":[subQ1,subQ0]});Q35=makeQuery(id+"F3.imprint","IMPRINT",FACE,{"disambiguationData":[TD([[makeQuery(id+"F3.imprint","IMPRINT",EDGE,{"disambiguationData":[TD([[subQ2,1.0]])],"derivedFrom":subQ1}),-1.0]])]});}
            var Q36;
            Q36=makeQuery(id+"F3.imprint","IMPRINT",FACE,{"disambiguationData":[TD([[makeQuery(id+"F3.imprint","IMPRINT",EDGE,{"derivedFrom":makeQuery(id+"F1.opExtrude","CAP_EDGE",EDGE,{"disambiguationData":[OSD([sQuery(id+"F0.wireOp",EDGE,"E10")])],"isStart":false})}),-1.0]])]});
            var Q37;
            {var subQ0=sQuery(id+"F3.wireOp",EDGE,"E76.trimOffspring");var subQ1=sQuery(id+"F3.wireOp",EDGE,"E68.trimOffspring");var subQ2=makeQuery(id+"F3.imprint","INTERSECT",VERTEX,{"derivedFrom":[subQ1,subQ0]});Q37=makeQuery(id+"F3.imprint","IMPRINT",FACE,{"disambiguationData":[TD([[makeQuery(id+"F3.imprint","IMPRINT",EDGE,{"disambiguationData":[TD([[subQ2,-1.0]])],"derivedFrom":subQ1}),-1.0]])]});}
            var Q38;
            {var subQ0=sQuery(id+"F3.wireOp",EDGE,"E79");Q38=makeQuery(id+"F3.imprint","IMPRINT",FACE,{"disambiguationData":[TD([[makeQuery(id+"F3.imprint","IMPRINT",EDGE,{"derivedFrom":subQ0}),-1.0]])]});}
            var Q39;
            Q39=makeQuery(id+"F3.imprint","IMPRINT",FACE,{"disambiguationData":[TD([[makeQuery(id+"F3.imprint","IMPRINT",EDGE,{"derivedFrom":makeQuery(id+"F1.opExtrude","CAP_EDGE",EDGE,{"disambiguationData":[OSD([sQuery(id+"F0.wireOp",EDGE,"E11.1.0.0")])],"isStart":false})}),-1.0]])]});
            var Q40;
            {var subQ0=sQuery(id+"F3.wireOp",EDGE,"E75.trimOffspring");var subQ1=sQuery(id+"F3.wireOp",EDGE,"E69.trimOffspring");var subQ2=makeQuery(id+"F3.imprint","INTERSECT",VERTEX,{"derivedFrom":[subQ1,subQ0]});Q40=makeQuery(id+"F3.imprint","IMPRINT",FACE,{"disambiguationData":[TD([[makeQuery(id+"F3.imprint","IMPRINT",EDGE,{"disambiguationData":[TD([[subQ2,-1.0]])],"derivedFrom":subQ1}),-1.0]])]});}
            var Q41;
            {var subQ0=sQuery(id+"F3.wireOp",EDGE,"E74.trimOffspring");var subQ1=sQuery(id+"F3.wireOp",EDGE,"E69.trimOffspring");var subQ2=makeQuery(id+"F3.imprint","INTERSECT",VERTEX,{"derivedFrom":[subQ1,subQ0]});Q41=makeQuery(id+"F3.imprint","IMPRINT",FACE,{"disambiguationData":[TD([[makeQuery(id+"F3.imprint","IMPRINT",EDGE,{"disambiguationData":[TD([[subQ2,1.0]])],"derivedFrom":subQ1}),-1.0]])]});}
            var Q42;
            Q42=makeQuery(id+"F3.imprint","IMPRINT",FACE,{"disambiguationData":[TD([[makeQuery(id+"F3.imprint","IMPRINT",EDGE,{"derivedFrom":makeQuery(id+"F1.opExtrude","CAP_EDGE",EDGE,{"disambiguationData":[OSD([sQuery(id+"F0.wireOp",EDGE,"E11.2.0.0")])],"isStart":false})}),-1.0]])]});
            var Q43;
            {var subQ0=sQuery(id+"F3.wireOp",EDGE,"E83.trimOffspring");var subQ1=sQuery(id+"F3.wireOp",EDGE,"E73.trimOffspring");var subQ2=makeQuery(id+"F3.imprint","INTERSECT",VERTEX,{"derivedFrom":[subQ1,subQ0]});Q43=makeQuery(id+"F3.imprint","IMPRINT",FACE,{"disambiguationData":[TD([[makeQuery(id+"F3.imprint","IMPRINT",EDGE,{"disambiguationData":[TD([[subQ2,-1.0]])],"derivedFrom":subQ1}),1.0]])]});}
            var Q44;
            {var subQ0=sQuery(id+"F3.wireOp",EDGE,"E83.trimOffspring");var subQ1=sQuery(id+"F3.wireOp",EDGE,"E71.trimOffspring");var subQ2=makeQuery(id+"F3.imprint","INTERSECT",VERTEX,{"derivedFrom":[subQ1,subQ0]});Q44=makeQuery(id+"F3.imprint","IMPRINT",FACE,{"disambiguationData":[TD([[makeQuery(id+"F3.imprint","IMPRINT",EDGE,{"disambiguationData":[TD([[subQ2,-1.0]])],"derivedFrom":subQ1}),-1.0]])]});}
            var Q45;
            {var subQ0=sQuery(id+"F3.wireOp",EDGE,"E72.trimOffspring");var subQ1=sQuery(id+"F3.wireOp",EDGE,"E70.trimOffspring");var subQ2=makeQuery(id+"F3.imprint","INTERSECT",VERTEX,{"derivedFrom":[subQ1,subQ0]});Q45=makeQuery(id+"F3.imprint","IMPRINT",FACE,{"disambiguationData":[TD([[makeQuery(id+"F3.imprint","IMPRINT",EDGE,{"disambiguationData":[TD([[subQ2,-1.0]])],"derivedFrom":subQ1}),-1.0]])]});}
            var Q46;
            {var subQ1=sQuery(id+"F3.wireOp",EDGE,"E24.5");Q46=makeQuery(id+"F3.imprint","IMPRINT",FACE,{"disambiguationData":[TD([[makeQuery(id+"F3.imprint","IMPRINT",EDGE,{"derivedFrom":subQ1}),1.0]])]});}
            var Q47;
            Q47=makeQuery(id+"F3.imprint","IMPRINT",FACE,{"disambiguationData":[TD([[makeQuery(id+"F3.imprint","IMPRINT",EDGE,{"derivedFrom":makeQuery(id+"F1.opExtrude","CAP_EDGE",EDGE,{"disambiguationData":[OSD([sQuery(id+"F0.wireOp",EDGE,"E21.MirrorC")])],"isStart":false})}),1.0]])]});
            var Q48;
            {var subQ0=sQuery(id+"F3.wireOp",EDGE,"E64.trimOffspring");var subQ1=sQuery(id+"F3.wireOp",EDGE,"E58.trimOffspring");var subQ2=makeQuery(id+"F3.imprint","INTERSECT",VERTEX,{"derivedFrom":[subQ1,subQ0]});Q48=makeQuery(id+"F3.imprint","IMPRINT",FACE,{"disambiguationData":[TD([[makeQuery(id+"F3.imprint","IMPRINT",EDGE,{"disambiguationData":[TD([[subQ2,1.0]])],"derivedFrom":subQ1}),1.0]])]});}
            var Q49;
            {var subQ0=sQuery(id+"F3.wireOp",EDGE,"E63.trimOffspring");var subQ1=sQuery(id+"F3.wireOp",EDGE,"E58.trimOffspring");var subQ2=makeQuery(id+"F3.imprint","INTERSECT",VERTEX,{"derivedFrom":[subQ1,subQ0]});Q49=makeQuery(id+"F3.imprint","IMPRINT",FACE,{"disambiguationData":[TD([[makeQuery(id+"F3.imprint","IMPRINT",EDGE,{"disambiguationData":[TD([[subQ2,-1.0]])],"derivedFrom":subQ1}),1.0]])]});}
            var Q50;
            {var subQ0=sQuery(id+"F3.wireOp",EDGE,"E65.trimOffspring");var subQ1=sQuery(id+"F3.wireOp",EDGE,"E57.trimOffspring");var subQ2=makeQuery(id+"F3.imprint","INTERSECT",VERTEX,{"derivedFrom":[subQ1,subQ0]});Q50=makeQuery(id+"F3.imprint","IMPRINT",FACE,{"disambiguationData":[TD([[makeQuery(id+"F3.imprint","IMPRINT",EDGE,{"disambiguationData":[TD([[subQ2,1.0]])],"derivedFrom":subQ1}),-1.0]])]});}
            var Q51;
            {var subQ0=sQuery(id+"F3.wireOp",EDGE,"E65.trimOffspring");var subQ1=sQuery(id+"F3.wireOp",EDGE,"E56.trimOffspring");var subQ2=makeQuery(id+"F3.imprint","INTERSECT",VERTEX,{"derivedFrom":[subQ1,subQ0]});Q51=makeQuery(id+"F3.imprint","IMPRINT",FACE,{"disambiguationData":[TD([[makeQuery(id+"F3.imprint","IMPRINT",EDGE,{"disambiguationData":[TD([[subQ2,1.0]])],"derivedFrom":subQ1}),1.0]])]});}
            var Q52;
            Q52=makeQuery(id+"F3.imprint","IMPRINT",FACE,{"disambiguationData":[TD([[makeQuery(id+"F3.imprint","IMPRINT",EDGE,{"derivedFrom":makeQuery(id+"F1.opExtrude","CAP_EDGE",EDGE,{"disambiguationData":[OSD([sQuery(id+"F0.wireOp",EDGE,"E8.2.0.0")])],"isStart":false})}),-1.0]])]});
            var Q53;
            {var subQ0=sQuery(id+"F3.wireOp",EDGE,"E81.trimOffspring");var subQ1=sQuery(id+"F3.wireOp",EDGE,"E56.trimOffspring");var subQ2=makeQuery(id+"F3.imprint","INTERSECT",VERTEX,{"derivedFrom":[subQ1,subQ0]});Q53=makeQuery(id+"F3.imprint","IMPRINT",FACE,{"disambiguationData":[TD([[makeQuery(id+"F3.imprint","IMPRINT",EDGE,{"disambiguationData":[TD([[subQ2,-1.0]])],"derivedFrom":subQ1}),1.0]])]});}
            var Q54;
            {var subQ0=sQuery(id+"F3.wireOp",EDGE,"E81.trimOffspring");var subQ1=sQuery(id+"F3.wireOp",EDGE,"E57.trimOffspring");var subQ2=makeQuery(id+"F3.imprint","INTERSECT",VERTEX,{"derivedFrom":[subQ1,subQ0]});Q54=makeQuery(id+"F3.imprint","IMPRINT",FACE,{"disambiguationData":[TD([[makeQuery(id+"F3.imprint","IMPRINT",EDGE,{"disambiguationData":[TD([[subQ2,-1.0]])],"derivedFrom":subQ1}),-1.0]])]});}
            var Q55;
            {var subQ0=sQuery(id+"F3.wireOp",EDGE,"E66.trimOffspring");var subQ1=sQuery(id+"F3.wireOp",EDGE,"E55.trimOffspring");var subQ2=makeQuery(id+"F3.imprint","INTERSECT",VERTEX,{"derivedFrom":[subQ1,subQ0]});Q55=makeQuery(id+"F3.imprint","IMPRINT",FACE,{"disambiguationData":[TD([[makeQuery(id+"F3.imprint","IMPRINT",EDGE,{"disambiguationData":[TD([[subQ2,1.0]])],"derivedFrom":subQ1}),-1.0]])]});}
            var Q56;
            {var subQ0=sQuery(id+"F3.wireOp",EDGE,"E66.trimOffspring");var subQ1=sQuery(id+"F3.wireOp",EDGE,"E54.trimOffspring");var subQ2=makeQuery(id+"F3.imprint","INTERSECT",VERTEX,{"derivedFrom":[subQ1,subQ0]});Q56=makeQuery(id+"F3.imprint","IMPRINT",FACE,{"disambiguationData":[TD([[makeQuery(id+"F3.imprint","IMPRINT",EDGE,{"disambiguationData":[TD([[subQ2,1.0]])],"derivedFrom":subQ1}),1.0]])]});}
            var Q57;
            {var subQ0=sQuery(id+"F3.wireOp",EDGE,"E62.trimOffspring");var subQ1=sQuery(id+"F3.wireOp",EDGE,"E54.trimOffspring");var subQ2=makeQuery(id+"F3.imprint","INTERSECT",VERTEX,{"derivedFrom":[subQ1,subQ0]});Q57=makeQuery(id+"F3.imprint","IMPRINT",FACE,{"disambiguationData":[TD([[makeQuery(id+"F3.imprint","IMPRINT",EDGE,{"disambiguationData":[TD([[subQ2,-1.0]])],"derivedFrom":subQ1}),1.0]])]});}
            var Q58;
            {var subQ0=sQuery(id+"F3.wireOp",EDGE,"E62.trimOffspring");var subQ1=sQuery(id+"F3.wireOp",EDGE,"E55.trimOffspring");var subQ2=makeQuery(id+"F3.imprint","INTERSECT",VERTEX,{"derivedFrom":[subQ1,subQ0]});Q58=makeQuery(id+"F3.imprint","IMPRINT",FACE,{"disambiguationData":[TD([[makeQuery(id+"F3.imprint","IMPRINT",EDGE,{"disambiguationData":[TD([[subQ2,-1.0]])],"derivedFrom":subQ1}),-1.0]])]});}
            var Q59;
            Q59=makeQuery(id+"F3.imprint","IMPRINT",FACE,{"disambiguationData":[TD([[makeQuery(id+"F3.imprint","IMPRINT",EDGE,{"derivedFrom":makeQuery(id+"F1.opExtrude","CAP_EDGE",EDGE,{"disambiguationData":[OSD([sQuery(id+"F0.wireOp",EDGE,"E8.1.0.0")])],"isStart":false})}),-1.0]])]});
            var Q60;
            Q60=makeQuery(id+"F3.imprint","IMPRINT",FACE,{"disambiguationData":[TD([[makeQuery(id+"F3.imprint","IMPRINT",EDGE,{"derivedFrom":makeQuery(id+"F1.opExtrude","CAP_EDGE",EDGE,{"disambiguationData":[OSD([sQuery(id+"F0.wireOp",EDGE,"E7")])],"isStart":false})}),-1.0]])]});
            var Q61;
            {var subQ0=sQuery(id+"F3.wireOp",EDGE,"E52.trimOffspring");var subQ1=sQuery(id+"F3.wireOp",EDGE,"E50.trimOffspring");var subQ2=makeQuery(id+"F3.imprint","INTERSECT",VERTEX,{"derivedFrom":[subQ1,subQ0]});Q61=makeQuery(id+"F3.imprint","IMPRINT",FACE,{"disambiguationData":[TD([[makeQuery(id+"F3.imprint","IMPRINT",EDGE,{"disambiguationData":[TD([[subQ2,-1.0]])],"derivedFrom":subQ1}),-1.0]])]});}
            var Q62;
            {var subQ0=sQuery(id+"F3.wireOp",EDGE,"E78");Q62=makeQuery(id+"F3.imprint","IMPRINT",FACE,{"disambiguationData":[TD([[makeQuery(id+"F3.imprint","IMPRINT",EDGE,{"derivedFrom":subQ0}),-1.0]])]});}
            var Q63;
            {var subQ0=sQuery(id+"F3.wireOp",EDGE,"E67.trimOffspring");var subQ1=sQuery(id+"F3.wireOp",EDGE,"E53.trimOffspring");var subQ2=makeQuery(id+"F3.imprint","INTERSECT",VERTEX,{"derivedFrom":[subQ1,subQ0]});Q63=makeQuery(id+"F3.imprint","IMPRINT",FACE,{"disambiguationData":[TD([[makeQuery(id+"F3.imprint","IMPRINT",EDGE,{"disambiguationData":[TD([[subQ2,1.0]])],"derivedFrom":subQ1}),-1.0]])]});}
            var Q64;
            {var subQ0=sQuery(id+"F3.wireOp",EDGE,"E67.trimOffspring");var subQ1=sQuery(id+"F3.wireOp",EDGE,"E52.trimOffspring");var subQ2=makeQuery(id+"F3.imprint","INTERSECT",VERTEX,{"derivedFrom":[subQ1,subQ0]});Q64=makeQuery(id+"F3.imprint","IMPRINT",FACE,{"disambiguationData":[TD([[makeQuery(id+"F3.imprint","IMPRINT",EDGE,{"disambiguationData":[TD([[subQ2,1.0]])],"derivedFrom":subQ1}),1.0]])]});}
            var Q65;
            Q65=makeQuery(id+"F3.imprint","IMPRINT",FACE,{"disambiguationData":[TD([[makeQuery(id+"F3.imprint","IMPRINT",EDGE,{"derivedFrom":makeQuery(id+"F1.opExtrude","CAP_EDGE",EDGE,{"disambiguationData":[OSD([sQuery(id+"F0.wireOp",EDGE,"E18")])],"isStart":false})}),-1.0]])]});
            var Q66;
            {var subQ0=sQuery(id+"F3.wireOp",EDGE,"E36.trimOffspring");var subQ1=sQuery(id+"F3.wireOp",EDGE,"E32.0.2.1");var subQ2=makeQuery(id+"F3.imprint","INTERSECT",VERTEX,{"derivedFrom":[subQ1,subQ0]});Q66=makeQuery(id+"F3.imprint","IMPRINT",FACE,{"disambiguationData":[TD([[makeQuery(id+"F3.imprint","IMPRINT",EDGE,{"disambiguationData":[TD([[subQ2,1.0]])],"derivedFrom":subQ1}),-1.0]])]});}
            var Q67;
            {var subQ0=sQuery(id+"F3.wireOp",EDGE,"E36.trimOffspring");var subQ1=sQuery(id+"F3.wireOp",EDGE,"E32.0.1.0");var subQ2=makeQuery(id+"F3.imprint","INTERSECT",VERTEX,{"derivedFrom":[subQ1,subQ0]});Q67=makeQuery(id+"F3.imprint","IMPRINT",FACE,{"disambiguationData":[TD([[makeQuery(id+"F3.imprint","IMPRINT",EDGE,{"disambiguationData":[TD([[subQ2,1.0]])],"derivedFrom":subQ1}),1.0]])]});}
            var Q68;
            {var subQ0=sQuery(id+"F3.wireOp",EDGE,"E31.1.0.0");var subQ1=sQuery(id+"F3.wireOp",EDGE,"E24.0");var subQ2=makeQuery(id+"F3.imprint","INTERSECT",VERTEX,{"derivedFrom":[subQ1,subQ0]});Q68=makeQuery(id+"F3.imprint","IMPRINT",FACE,{"disambiguationData":[TD([[makeQuery(id+"F3.imprint","IMPRINT",EDGE,{"disambiguationData":[TD([[subQ2,1.0]])],"derivedFrom":subQ1}),1.0]])]});}
            var Q69;
            {var subQ3=sQuery(id+"F3.wireOp",EDGE,"E24.11");Q69=makeQuery(id+"F3.imprint","IMPRINT",FACE,{"disambiguationData":[TD([[makeQuery(id+"F3.imprint","IMPRINT",EDGE,{"derivedFrom":subQ3}),-1.0]])]});}
            var Q70;
            {var subQ0=sQuery(id+"F3.wireOp",EDGE,"E29");var subQ1=sQuery(id+"F3.wireOp",EDGE,"E24.2");var subQ2=makeQuery(id+"F3.imprint","INTERSECT",VERTEX,{"derivedFrom":[subQ1,subQ0]});Q70=makeQuery(id+"F3.imprint","IMPRINT",FACE,{"disambiguationData":[TD([[makeQuery(id+"F3.imprint","IMPRINT",EDGE,{"disambiguationData":[TD([[subQ2,-1.0]])],"derivedFrom":subQ1}),-1.0]])]});}
            var Q71;
            {var subQ0=sQuery(id+"F3.wireOp",EDGE,"E31.2.0.0");var subQ1=sQuery(id+"F3.wireOp",EDGE,"E24.0");var subQ2=makeQuery(id+"F3.imprint","INTERSECT",VERTEX,{"derivedFrom":[subQ1,subQ0]});Q71=makeQuery(id+"F3.imprint","IMPRINT",FACE,{"disambiguationData":[TD([[makeQuery(id+"F3.imprint","IMPRINT",EDGE,{"disambiguationData":[TD([[subQ2,1.0]])],"derivedFrom":subQ1}),1.0]])]});}
            var Q72;
            {var subQ0=sQuery(id+"F3.wireOp",EDGE,"E25.right");Q72=makeQuery(id+"F3.imprint","IMPRINT",FACE,{"disambiguationData":[TD([[makeQuery(id+"F3.imprint","IMPRINT",EDGE,{"derivedFrom":subQ0}),1.0]])]});}
            var Q73;
            {var subQ0=sQuery(id+"F3.wireOp",EDGE,"E64.trimOffspring");var subQ1=sQuery(id+"F3.wireOp",EDGE,"E24.6");var subQ2=makeQuery(id+"F3.imprint","INTERSECT",VERTEX,{"derivedFrom":[subQ1,subQ0]});Q73=makeQuery(id+"F3.imprint","IMPRINT",FACE,{"disambiguationData":[TD([[makeQuery(id+"F3.imprint","IMPRINT",EDGE,{"disambiguationData":[TD([[subQ2,1.0]])],"derivedFrom":subQ1}),1.0]])]});}
            var Q74;
            {var subQ0=sQuery(id+"F3.wireOp",EDGE,"E71.trimOffspring");var subQ1=sQuery(id+"F3.wireOp",EDGE,"E24.4");var subQ2=makeQuery(id+"F3.imprint","INTERSECT",VERTEX,{"derivedFrom":[subQ1,subQ0]});Q74=makeQuery(id+"F3.imprint","IMPRINT",FACE,{"disambiguationData":[TD([[makeQuery(id+"F3.imprint","IMPRINT",EDGE,{"disambiguationData":[TD([[subQ2,1.0]])],"derivedFrom":subQ1}),-1.0]])]});}
            var Q75;
            {var subQ0=sQuery(id+"F3.wireOp",EDGE,"E73.trimOffspring");var subQ1=sQuery(id+"F3.wireOp",EDGE,"E24.4");var subQ2=makeQuery(id+"F3.imprint","INTERSECT",VERTEX,{"derivedFrom":[subQ1,subQ0]});Q75=makeQuery(id+"F3.imprint","IMPRINT",FACE,{"disambiguationData":[TD([[makeQuery(id+"F3.imprint","IMPRINT",EDGE,{"disambiguationData":[TD([[subQ2,-1.0]])],"derivedFrom":subQ1}),-1.0]])]});}
            var Q76;
            {var subQ0=sQuery(id+"F3.wireOp",EDGE,"E75.trimOffspring");var subQ1=sQuery(id+"F3.wireOp",EDGE,"E24.4");var subQ2=makeQuery(id+"F3.imprint","INTERSECT",VERTEX,{"derivedFrom":[subQ1,subQ0]});Q76=makeQuery(id+"F3.imprint","IMPRINT",FACE,{"disambiguationData":[TD([[makeQuery(id+"F3.imprint","IMPRINT",EDGE,{"disambiguationData":[TD([[subQ2,-1.0]])],"derivedFrom":subQ1}),-1.0]])]});}
            var Q77;
            {var subQ0=sQuery(id+"F3.wireOp",EDGE,"E76.trimOffspring");var subQ1=sQuery(id+"F3.wireOp",EDGE,"E24.4");var subQ2=makeQuery(id+"F3.imprint","INTERSECT",VERTEX,{"derivedFrom":[subQ1,subQ0]});Q77=makeQuery(id+"F3.imprint","IMPRINT",FACE,{"disambiguationData":[TD([[makeQuery(id+"F3.imprint","IMPRINT",EDGE,{"disambiguationData":[TD([[subQ2,-1.0]])],"derivedFrom":subQ1}),-1.0]])]});}
            var Q78;
            {var subQ0=sQuery(id+"F3.wireOp",EDGE,"E43.trimOffspring");var subQ1=sQuery(id+"F3.wireOp",EDGE,"E24.9");var subQ2=makeQuery(id+"F3.imprint","INTERSECT",VERTEX,{"derivedFrom":[subQ1,subQ0]});Q78=makeQuery(id+"F3.imprint","IMPRINT",FACE,{"disambiguationData":[TD([[makeQuery(id+"F3.imprint","IMPRINT",EDGE,{"disambiguationData":[TD([[subQ2,-1.0]])],"derivedFrom":subQ1}),-1.0]])]});}
            var Q79;
            {var subQ0=sQuery(id+"F3.wireOp",EDGE,"E59.trimOffspring");var subQ1=sQuery(id+"F3.wireOp",EDGE,"E24.13");var subQ2=makeQuery(id+"F3.imprint","INTERSECT",VERTEX,{"derivedFrom":[subQ1,subQ0]});Q79=makeQuery(id+"F3.imprint","IMPRINT",FACE,{"disambiguationData":[TD([[makeQuery(id+"F3.imprint","IMPRINT",EDGE,{"disambiguationData":[TD([[subQ2,1.0]])],"derivedFrom":subQ1}),-1.0]])]});}
            var Q80;
            {var subQ0=sQuery(id+"F3.wireOp",EDGE,"E66.trimOffspring");var subQ1=sQuery(id+"F3.wireOp",EDGE,"E24.17");var subQ2=makeQuery(id+"F3.imprint","INTERSECT",VERTEX,{"derivedFrom":[subQ1,subQ0]});Q80=makeQuery(id+"F3.imprint","IMPRINT",FACE,{"disambiguationData":[TD([[makeQuery(id+"F3.imprint","IMPRINT",EDGE,{"disambiguationData":[TD([[subQ2,-1.0]])],"derivedFrom":subQ1}),-1.0]])]});}
            var Q81;
            {var subQ0=sQuery(id+"F3.wireOp",EDGE,"E32.0.1.0");var subQ1=sQuery(id+"F3.wireOp",EDGE,"E24.2");var subQ2=makeQuery(id+"F3.imprint","INTERSECT",VERTEX,{"derivedFrom":[subQ1,subQ0]});Q81=makeQuery(id+"F3.imprint","IMPRINT",FACE,{"disambiguationData":[TD([[makeQuery(id+"F3.imprint","IMPRINT",EDGE,{"disambiguationData":[TD([[subQ2,1.0]])],"derivedFrom":subQ1}),-1.0]])]});}
            var Q82;
            {var subQ0=sQuery(id+"F3.wireOp",EDGE,"E61.trimOffspring");var subQ1=sQuery(id+"F3.wireOp",EDGE,"E24.6");var subQ2=makeQuery(id+"F3.imprint","INTERSECT",VERTEX,{"derivedFrom":[subQ1,subQ0]});Q82=makeQuery(id+"F3.imprint","IMPRINT",FACE,{"disambiguationData":[TD([[makeQuery(id+"F3.imprint","IMPRINT",EDGE,{"disambiguationData":[TD([[subQ2,1.0]])],"derivedFrom":subQ1}),1.0]])]});}
            var Q83;
            {var subQ5=sQuery(id+"F3.wireOp",EDGE,"E84.trimOffspring");Q83=makeQuery(id+"F3.imprint","IMPRINT",FACE,{"disambiguationData":[TD([[makeQuery(id+"F3.imprint","IMPRINT",EDGE,{"derivedFrom":subQ5}),-1.0]])]});}
            var Q84;
            {var subQ0=sQuery(id+"F3.wireOp",EDGE,"E31.3.0.0");var subQ1=sQuery(id+"F3.wireOp",EDGE,"E24.0");var subQ2=makeQuery(id+"F3.imprint","INTERSECT",VERTEX,{"derivedFrom":[subQ1,subQ0]});Q84=makeQuery(id+"F3.imprint","IMPRINT",FACE,{"disambiguationData":[TD([[makeQuery(id+"F3.imprint","IMPRINT",EDGE,{"disambiguationData":[TD([[subQ2,1.0]])],"derivedFrom":subQ1}),1.0]])]});}
            extrude(context, id + "F4", {"entities" : qUnion([Q0, Q1, Q2, Q3, Q4, Q5, Q6, Q7, Q8, Q9, Q10, Q11, Q12, Q13, Q14, Q15, Q16, Q17, Q18, Q19, Q20, Q21, Q22, Q23, Q24, Q25, Q26, Q27, Q28, Q29, Q30, Q31, Q32, Q33, Q34, Q35, Q36, Q37, Q38, Q39, Q40, Q41, Q42, Q43, Q44, Q45, Q46, Q47, Q48, Q49, Q50, Q51, Q52, Q53, Q54, Q55, Q56, Q57, Q58, Q59, Q60, Q61, Q62, Q63, Q64, Q65, Q66, Q67, Q68, Q69, Q70, Q71, Q72, Q73, Q74, Q75, Q76, Q77, Q78, Q79, Q80, Q81, Q82, Q83, Q84]), "operationType" : NewBodyOperationType.ADD, "depth" : 2 * mm});
        }
        {
            var Q0;
            Q0=makeQuery(id+"F4.opExtrude","SWEPT_EDGE",EDGE,{"disambiguationData":[OSD([sQuery(id+"F3.wireOp",EDGE,"E27"),sQuery(id+"F3.wireOp",EDGE,"E32.0.2.0")])]});
            var Q1;
            Q1=makeQuery(id+"F4.opExtrude","SWEPT_EDGE",EDGE,{"disambiguationData":[OSD([sQuery(id+"F3.wireOp",EDGE,"E28.MirrorCS"),sQuery(id+"F3.wireOp",EDGE,"E34.trimOffspring")])]});
            var Q2;
            Q2=makeQuery(id+"F4.opExtrude","SWEPT_EDGE",EDGE,{"disambiguationData":[OSD([sQuery(id+"F3.wireOp",EDGE,"E31.1.0.0"),sQuery(id+"F3.wireOp",EDGE,"E34.trimOffspring")])]});
            var Q3;
            Q3=makeQuery(id+"F4.opExtrude","SWEPT_EDGE",EDGE,{"disambiguationData":[OSD([sQuery(id+"F3.wireOp",EDGE,"E31.1.0.1"),sQuery(id+"F3.wireOp",EDGE,"E43.trimOffspring")])]});
            var Q4;
            Q4=makeQuery(id+"F4.opExtrude","SWEPT_EDGE",EDGE,{"disambiguationData":[OSD([sQuery(id+"F3.wireOp",EDGE,"E31.2.0.0"),sQuery(id+"F3.wireOp",EDGE,"E43.trimOffspring")])]});
            var Q5;
            Q5=makeQuery(id+"F4.opExtrude","SWEPT_EDGE",EDGE,{"disambiguationData":[OSD([sQuery(id+"F3.wireOp",EDGE,"E31.2.0.1"),sQuery(id+"F3.wireOp",EDGE,"E44.trimOffspring")])]});
            var Q6;
            Q6=makeQuery(id+"F4.opExtrude","SWEPT_EDGE",EDGE,{"disambiguationData":[OSD([sQuery(id+"F3.wireOp",EDGE,"E31.3.0.0"),sQuery(id+"F3.wireOp",EDGE,"E44.trimOffspring")])]});
            var Q7;
            Q7=makeQuery(id+"F4.opExtrude","SWEPT_EDGE",EDGE,{"disambiguationData":[OSD([sQuery(id+"F3.wireOp",EDGE,"E31.3.0.1"),sQuery(id+"F3.wireOp",EDGE,"E45.trimOffspring")])]});
            var Q8;
            Q8=makeQuery(id+"F4.opExtrude","SWEPT_EDGE",EDGE,{"disambiguationData":[OSD([sQuery(id+"F3.wireOp",EDGE,"E42.trimOffspring"),sQuery(id+"F3.wireOp",EDGE,"E61.trimOffspring")])]});
            var Q9;
            Q9=makeQuery(id+"F4.opExtrude","SWEPT_EDGE",EDGE,{"disambiguationData":[OSD([sQuery(id+"F3.wireOp",EDGE,"E41.trimOffspring"),sQuery(id+"F3.wireOp",EDGE,"E60.trimOffspring")])]});
            var Q10;
            Q10=makeQuery(id+"F4.opExtrude","SWEPT_EDGE",EDGE,{"disambiguationData":[OSD([sQuery(id+"F3.wireOp",EDGE,"E40.trimOffspring"),sQuery(id+"F3.wireOp",EDGE,"E60.trimOffspring")])]});
            var Q11;
            Q11=makeQuery(id+"F4.opExtrude","SWEPT_EDGE",EDGE,{"disambiguationData":[OSD([sQuery(id+"F3.wireOp",EDGE,"E39.trimOffspring"),sQuery(id+"F3.wireOp",EDGE,"E59.trimOffspring")])]});
            var Q12;
            Q12=makeQuery(id+"F4.opExtrude","SWEPT_EDGE",EDGE,{"disambiguationData":[OSD([sQuery(id+"F3.wireOp",EDGE,"E37.trimOffspring"),sQuery(id+"F3.wireOp",EDGE,"E49.trimOffspring")])]});
            var Q13;
            Q13=makeQuery(id+"F4.opExtrude","SWEPT_EDGE",EDGE,{"disambiguationData":[OSD([sQuery(id+"F3.wireOp",EDGE,"E38.trimOffspring"),sQuery(id+"F3.wireOp",EDGE,"E59.trimOffspring")])]});
            var Q14;
            Q14=makeQuery(id+"F4.opExtrude","SWEPT_EDGE",EDGE,{"disambiguationData":[OSD([sQuery(id+"F3.wireOp",EDGE,"E32.0.1.0"),sQuery(id+"F3.wireOp",EDGE,"E36.trimOffspring")])]});
            var Q15;
            Q15=makeQuery(id+"F4.opExtrude","SWEPT_EDGE",EDGE,{"disambiguationData":[OSD([sQuery(id+"F3.wireOp",EDGE,"E35.trimOffspring"),sQuery(id+"F3.wireOp",EDGE,"E49.trimOffspring")])]});
            var Q16;
            Q16=makeQuery(id+"F4.opExtrude","SWEPT_EDGE",EDGE,{"disambiguationData":[OSD([sQuery(id+"F3.wireOp",EDGE,"E32.0.1.1"),sQuery(id+"F3.wireOp",EDGE,"E51.trimOffspring")])]});
            var Q17;
            Q17=makeQuery(id+"F4.opExtrude","SWEPT_EDGE",EDGE,{"disambiguationData":[OSD([sQuery(id+"F3.wireOp",EDGE,"E30.MirrorCS"),sQuery(id+"F3.wireOp",EDGE,"E51.trimOffspring")])]});
            var Q18;
            Q18=makeQuery(id+"F4.opExtrude","SWEPT_EDGE",EDGE,{"disambiguationData":[OSD([sQuery(id+"F3.wireOp",EDGE,"E52.trimOffspring"),sQuery(id+"F3.wireOp",EDGE,"E67.trimOffspring")])]});
            var Q19;
            Q19=makeQuery(id+"F4.opExtrude","SWEPT_EDGE",EDGE,{"disambiguationData":[OSD([sQuery(id+"F3.wireOp",EDGE,"E53.trimOffspring"),sQuery(id+"F3.wireOp",EDGE,"E67.trimOffspring")])]});
            var Q20;
            Q20=makeQuery(id+"F4.opExtrude","SWEPT_EDGE",EDGE,{"disambiguationData":[OSD([sQuery(id+"F3.wireOp",EDGE,"E53.trimOffspring"),sQuery(id+"F3.wireOp",EDGE,"E78")])]});
            var Q21;
            Q21=makeQuery(id+"F4.opExtrude","SWEPT_EDGE",EDGE,{"disambiguationData":[OSD([sQuery(id+"F3.wireOp",EDGE,"E54.trimOffspring"),sQuery(id+"F3.wireOp",EDGE,"E66.trimOffspring")])]});
            var Q22;
            Q22=makeQuery(id+"F4.opExtrude","SWEPT_EDGE",EDGE,{"disambiguationData":[OSD([sQuery(id+"F3.wireOp",EDGE,"E55.trimOffspring"),sQuery(id+"F3.wireOp",EDGE,"E66.trimOffspring")])]});
            var Q23;
            Q23=makeQuery(id+"F4.opExtrude","SWEPT_EDGE",EDGE,{"disambiguationData":[OSD([sQuery(id+"F3.wireOp",EDGE,"E55.trimOffspring"),sQuery(id+"F3.wireOp",EDGE,"E62.trimOffspring")])]});
            var Q24;
            Q24=makeQuery(id+"F4.opExtrude","SWEPT_EDGE",EDGE,{"disambiguationData":[OSD([sQuery(id+"F3.wireOp",EDGE,"E56.trimOffspring"),sQuery(id+"F3.wireOp",EDGE,"E65.trimOffspring")])]});
            var Q25;
            Q25=makeQuery(id+"F4.opExtrude","SWEPT_EDGE",EDGE,{"disambiguationData":[OSD([sQuery(id+"F3.wireOp",EDGE,"E57.trimOffspring"),sQuery(id+"F3.wireOp",EDGE,"E65.trimOffspring")])]});
            var Q26;
            Q26=makeQuery(id+"F4.opExtrude","SWEPT_EDGE",EDGE,{"disambiguationData":[OSD([sQuery(id+"F3.wireOp",EDGE,"E58.trimOffspring"),sQuery(id+"F3.wireOp",EDGE,"E64.trimOffspring")])]});
            var Q27;
            Q27=makeQuery(id+"F4.opExtrude","SWEPT_EDGE",EDGE,{"disambiguationData":[OSD([sQuery(id+"F3.wireOp",EDGE,"E57.trimOffspring"),sQuery(id+"F3.wireOp",EDGE,"E81.trimOffspring")])]});
            var Q28;
            Q28=makeQuery(id+"F4.opExtrude","SWEPT_EDGE",EDGE,{"disambiguationData":[OSD([sQuery(id+"F3.wireOp",EDGE,"E71.trimOffspring"),sQuery(id+"F3.wireOp",EDGE,"E83.trimOffspring")])]});
            var Q29;
            Q29=makeQuery(id+"F4.opExtrude","SWEPT_EDGE",EDGE,{"disambiguationData":[OSD([sQuery(id+"F3.wireOp",EDGE,"E29"),sQuery(id+"F3.wireOp",EDGE,"E77.trimOffspring")])]});
            var Q30;
            Q30=makeQuery(id+"F4.opExtrude","SWEPT_EDGE",EDGE,{"disambiguationData":[OSD([sQuery(id+"F3.wireOp",EDGE,"E68.trimOffspring"),sQuery(id+"F3.wireOp",EDGE,"E76.trimOffspring")])]});
            var Q31;
            Q31=makeQuery(id+"F4.opExtrude","SWEPT_EDGE",EDGE,{"disambiguationData":[OSD([sQuery(id+"F3.wireOp",EDGE,"E79"),sQuery(id+"F3.wireOp",EDGE,"E80.trimOffspring")])]});
            var Q32;
            Q32=makeQuery(id+"F4.opExtrude","SWEPT_EDGE",EDGE,{"disambiguationData":[OSD([sQuery(id+"F3.wireOp",EDGE,"E69.trimOffspring"),sQuery(id+"F3.wireOp",EDGE,"E75.trimOffspring")])]});
            var Q33;
            Q33=makeQuery(id+"F4.opExtrude","SWEPT_EDGE",EDGE,{"disambiguationData":[OSD([sQuery(id+"F3.wireOp",EDGE,"E69.trimOffspring"),sQuery(id+"F3.wireOp",EDGE,"E74.trimOffspring")])]});
            var Q34;
            Q34=makeQuery(id+"F4.opExtrude","SWEPT_EDGE",EDGE,{"disambiguationData":[OSD([sQuery(id+"F3.wireOp",EDGE,"E73.trimOffspring"),sQuery(id+"F3.wireOp",EDGE,"E83.trimOffspring")])]});
            var Q35;
            Q35=makeQuery(id+"F4.opExtrude","SWEPT_EDGE",EDGE,{"disambiguationData":[OSD([sQuery(id+"F3.wireOp",EDGE,"E70.trimOffspring"),sQuery(id+"F3.wireOp",EDGE,"E72.trimOffspring")])]});
            var Q36;
            Q36=makeQuery(id+"F4.opExtrude","SWEPT_EDGE",EDGE,{"disambiguationData":[OSD([sQuery(id+"F3.wireOp",EDGE,"E58.trimOffspring"),sQuery(id+"F3.wireOp",EDGE,"E63.trimOffspring")])]});
            var Q37;
            Q37=makeQuery(id+"F4.opExtrude","SWEPT_EDGE",EDGE,{"disambiguationData":[OSD([sQuery(id+"F3.wireOp",EDGE,"E56.trimOffspring"),sQuery(id+"F3.wireOp",EDGE,"E81.trimOffspring")])]});
            var Q38;
            Q38=makeQuery(id+"F4.opExtrude","SWEPT_EDGE",EDGE,{"disambiguationData":[OSD([sQuery(id+"F3.wireOp",EDGE,"E54.trimOffspring"),sQuery(id+"F3.wireOp",EDGE,"E62.trimOffspring")])]});
            var Q39;
            Q39=makeQuery(id+"F4.opExtrude","SWEPT_EDGE",EDGE,{"disambiguationData":[OSD([sQuery(id+"F3.wireOp",EDGE,"E50.trimOffspring"),sQuery(id+"F3.wireOp",EDGE,"E52.trimOffspring")])]});
            var Q40;
            Q40=makeQuery(id+"F4.opExtrude","SWEPT_EDGE",EDGE,{"disambiguationData":[OSD([sQuery(id+"F3.wireOp",EDGE,"E40.trimOffspring"),sQuery(id+"F3.wireOp",EDGE,"E47.trimOffspring")])]});
            var Q41;
            Q41=makeQuery(id+"F4.opExtrude","SWEPT_EDGE",EDGE,{"disambiguationData":[OSD([sQuery(id+"F3.wireOp",EDGE,"E41.trimOffspring"),sQuery(id+"F3.wireOp",EDGE,"E47.trimOffspring")])]});
            var Q42;
            Q42=makeQuery(id+"F4.opExtrude","SWEPT_EDGE",EDGE,{"disambiguationData":[OSD([sQuery(id+"F3.wireOp",EDGE,"E42.trimOffspring"),sQuery(id+"F3.wireOp",EDGE,"E46.trimOffspring")])]});
            var Q43;
            Q43=makeQuery(id+"F4.opExtrude","SWEPT_EDGE",EDGE,{"disambiguationData":[OSD([sQuery(id+"F3.wireOp",EDGE,"E39.trimOffspring"),sQuery(id+"F3.wireOp",EDGE,"E48.trimOffspring")])]});
            var Q44;
            Q44=makeQuery(id+"F4.opExtrude","SWEPT_EDGE",EDGE,{"disambiguationData":[OSD([sQuery(id+"F3.wireOp",EDGE,"E32.0.2.1"),sQuery(id+"F3.wireOp",EDGE,"E36.trimOffspring")])]});
            var Q45;
            Q45=makeQuery(id+"F4.opExtrude","SWEPT_EDGE",EDGE,{"disambiguationData":[OSD([sQuery(id+"F3.wireOp",EDGE,"E33.trimOffspring"),sQuery(id+"F3.wireOp",EDGE,"E35.trimOffspring")])]});
            var Q46;
            Q46=makeQuery(id+"F4.opExtrude","SWEPT_EDGE",EDGE,{"disambiguationData":[OSD([sQuery(id+"F3.wireOp",EDGE,"E33.trimOffspring"),sQuery(id+"F3.wireOp",EDGE,"E37.trimOffspring")])]});
            var Q47;
            Q47=makeQuery(id+"F4.opExtrude","SWEPT_EDGE",EDGE,{"disambiguationData":[OSD([sQuery(id+"F3.wireOp",EDGE,"E38.trimOffspring"),sQuery(id+"F3.wireOp",EDGE,"E48.trimOffspring")])]});
            fillet(context, id + "F5", {"entities" : qUnion([Q0, Q1, Q2, Q3, Q4, Q5, Q6, Q7, Q8, Q9, Q10, Q11, Q12, Q13, Q14, Q15, Q16, Q17, Q18, Q19, Q20, Q21, Q22, Q23, Q24, Q25, Q26, Q27, Q28, Q29, Q30, Q31, Q32, Q33, Q34, Q35, Q36, Q37, Q38, Q39, Q40, Q41, Q42, Q43, Q44, Q45, Q46, Q47]), "radius" : 1 * mm, "tangentPropagation" : true, "conicFillet" : false});
        }
    });
